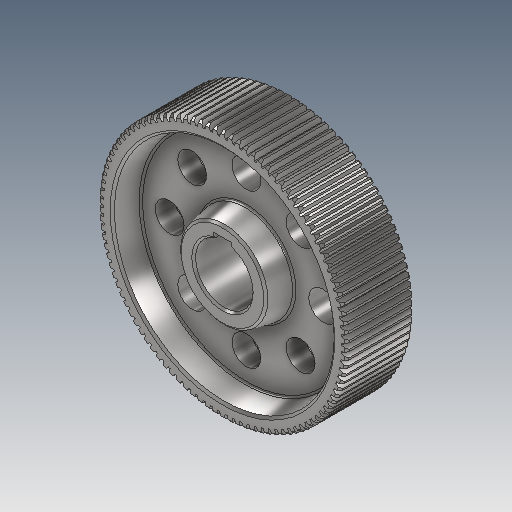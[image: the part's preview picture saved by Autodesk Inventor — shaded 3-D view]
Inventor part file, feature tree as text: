
AUTODESK INVENTOR PART (.ipt)
format: ipt  version: 2025 (Build 290162000, 162)  size: 1,377,792 bytes
history: native  units: mm (DEFAULTED — no unit token found)
features: sketch x6, extrude x5, plane x3, other x3, mirror x2, chamfer x1, fillet x1
ambient origin geometry x8: Origin, YZ Plane, XZ Plane, XY Plane, X Axis, Y Axis, Z Axis, Center Point
bodies: Solid1 (feature_tree)
feature tree (21):
  extrude  "Extrusion1"  Depth=70.0mm TaperAngle=0.0deg
  plane  "Work Plane2"
  plane  "Work Plane8"
  plane  "Work Plane9"
  other  "正齿轮"
  extrude  "拉伸2"  Depth=10.0mm TaperAngle=0.0deg
  extrude  "拉伸3"  Depth=0.307999mm TaperAngle=0.0deg
  mirror  "镜像1"
  extrude  "拉伸4"  TaperAngle=0.0deg  [1 undecoded]
  chamfer  "倒角1"  [1 undecoded]
  other  "轮毂键槽"
  fillet  "圆角1"  Radius=60.0mm
  extrude  "拉伸5"  Depth=18.0mm
  mirror  "镜像2"
  sketch  "Sketch1"  dims[d0=260.0mm d1=70.0mm d2=0.0mm]
  other  "Srf1"
  sketch  "草图3"  dims[d16=166.25mm d17=0.0mm d34=0.307999mm]
  sketch  "草图4"  dims[d39=0.0mm d41=0.0mm]
  sketch  "草图5"  dims[d43=166.25mm]
  sketch  "草图 - 环形阵列1"  dims[d3=255.0mm d4=10.0mm d5=0.0mm]
  sketch  "草图6"  dims[d46=166.25mm d47=0.0mm d48=0.0mm d49=60.0mm d50=18.0mm d51=11.0mm d52=18.0mm d53=0.0mm d54=90.0mm d55=230.0mm d56=25.0mm d57=-2.007129mm d58=30.0mm d60=80.0mm d62=360.0deg d64=70.0mm d65=0.0mm d66=2.0mm d67=2.0mm d68=45.0deg d69=2.0mm d70=160.0mm d71=2.5mm d72=70.0mm d73=-7.853982mm d74=2.5mm]
note: 2 required parameter values undecoded (feature->parameter linkage not recoverable at this tier; creation-order binding heuristic only, values carry confidence <= 0.55)
